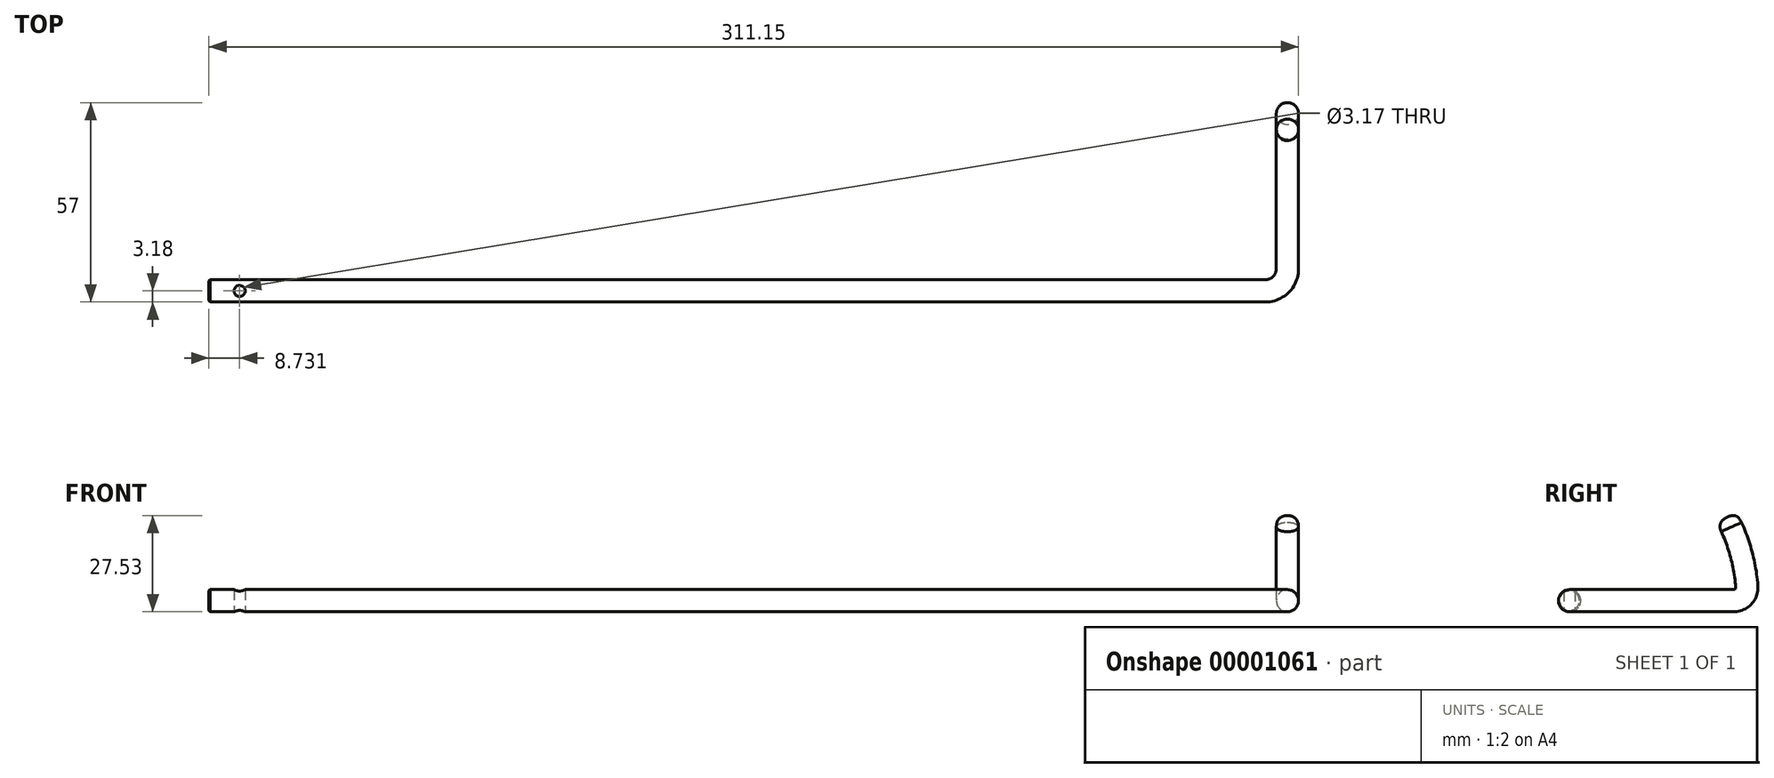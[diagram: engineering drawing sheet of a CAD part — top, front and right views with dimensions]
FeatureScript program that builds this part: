
annotation { "Feature Type Name" : "Feature", "Feature Type Description" : "" }
export const myFeature = defineFeature(function(context is Context, id is Id, definition is map)
    precondition{}
    {
        {
            var Q0;
            Q0=qCreatedBy(makeId("Top.planeOp"),FACE);
            var sketch = newSketch(context, id + "F0", { "sketchPlane" : qUnion([Q0])});
            skLineSegment(sketch, "E0", {"start": v(0, 0) * mm, "end": v(301.63, 0) * mm});
            skLineSegment(sketch, "E1", {"start": v(307.98, 6.35) * mm, "end": v(307.98, 50.8) * mm});
            skPoint(sketch, "E2.visualSharp", {"position": v(307.98, 0) * mm});
            skArc(sketch, "E2.filletArc", {"start": v(301.63, 0) * mm, "mid": v(306.12, 1.86) * mm, "end": v(307.98, 6.35) * mm});
            skLineSegment(sketch, "E3", {"start": v(307.98, 0) * mm, "end": v(301.63, 0) * mm, "construction": true});
            skSolve(sketch);
        }
        {
            var Q0;
            Q0=sQuery(id+"F0.wireOp",EDGE,"E3");
            var Q1;
            Q1=sQuery(id+"F0.wireOp",VERTEX,"E2.visualSharp");
            cPlane(context, id + "F1", {"entities" : qUnion([Q0, Q1]), "cplaneType" : CPlaneType.CURVE_POINT, "offset" : 152.4 * mm, "width" : 152.4 * mm, "height" : 152.4 * mm});
        }
        {
            var Q0;
            Q0=qCreatedBy(id+"F1.planeOp",FACE);
            var sketch = newSketch(context, id + "F2", { "sketchPlane" : qUnion([Q0])});
            skArc(sketch, "E4", {"start": v(-44.87, 23.81) * mm, "mid": v(-48.76, 14.26) * mm, "end": v(-50.63, 4.12) * mm});
            skArc(sketch, "E5", {"start": v(-50.63, 4.12) * mm, "mid": v(-49.64, 1.23) * mm, "end": v(-46.84, 0) * mm});
            skPoint(sketch, "E6.orphan", {"position": v(-50.8, 0) * mm});
            skSolve(sketch);
        }
        {
            var Q0;
            Q0=sQuery(id+"F2.wireOp",VERTEX,"E4.start");
            var Q1;
            Q1=sQuery(id+"F2.wireOp",EDGE,"E4");
            cPlane(context, id + "F3", {"entities" : qUnion([Q0, Q1]), "cplaneType" : CPlaneType.CURVE_POINT, "offset" : 152.4 * mm, "width" : 152.4 * mm, "height" : 152.4 * mm});
        }
        {
            var Q0;
            Q0=qCreatedBy(id+"F3.planeOp",FACE);
            var sketch = newSketch(context, id + "F4", { "sketchPlane" : qUnion([Q0])});
            skCircle(sketch, "E7", {"center": v(307.98, -50.8) * mm, "radius": 3.18 * mm});
            skSolve(sketch);
        }
        {
            var Q0;
            Q0=qCreatedBy(makeId("Right.planeOp"),FACE);
            var sketch = newSketch(context, id + "F5", { "sketchPlane" : qUnion([Q0])});
            skCircle(sketch, "E8", {"center": v(0, 0) * mm, "radius": 3.17 * mm});
            skSolve(sketch);
        }
        {
            var Q0;
            Q0=makeQuery(id+"F5.imprint","IMPRINT",FACE,{"disambiguationData":[TD([[makeQuery(id+"F5.imprint","IMPRINT",EDGE,{"derivedFrom":sQuery(id+"F5.wireOp",EDGE,"E8")}),1.0]])]});
            var Q1;
            Q1=sQuery(id+"F0.wireOp",EDGE,"E0");
            var Q2;
            Q2=sQuery(id+"F0.wireOp",EDGE,"E2.filletArc");
            sweep(context, id + "F6", {"profiles" : qUnion([Q0]), "path" : qUnion([Q1, Q2])});
        }
        {
            var Q0;
            Q0=makeQuery(id+"F4.imprint","IMPRINT",FACE,{"disambiguationData":[TD([[makeQuery(id+"F4.imprint","IMPRINT",EDGE,{"derivedFrom":sQuery(id+"F4.wireOp",EDGE,"E7")}),1.0]])]});
            var Q1;
            Q1=sQuery(id+"F2.wireOp",EDGE,"E4");
            var Q2;
            Q2=sQuery(id+"F2.wireOp",EDGE,"E5");
            sweep(context, id + "F7", {"profiles" : qUnion([Q0]), "path" : qUnion([Q1, Q2])});
        }
        {
            var Q0;
            Q0=makeQuery(id+"F7.opSweep","CAP_FACE",FACE,{"disambiguationData":[OSD([sQuery(id+"F2.wireOp",VERTEX,"E5.end"),sQuery(id+"F4.wireOp",EDGE,"E7")])],"isStart":false});
            extrude(context, id + "F8", {"entities" : qUnion([Q0]), "operationType" : NewBodyOperationType.ADD, "endBound" : BoundingType.UP_TO_NEXT, "depth" : 25.4 * mm});
        }
        {
            var Q0;
            Q0=makeQuery(id+"F7.opSweep","CAP_EDGE",EDGE,{"disambiguationData":[OSD([sQuery(id+"F2.wireOp",VERTEX,"E4.start"),sQuery(id+"F4.wireOp",EDGE,"E7")])],"isStart":true});
            fillet(context, id + "F9", {"entities" : qUnion([Q0]), "radius" : 3.05 * mm, "tangentPropagation" : true, "rho" : 0.5, "crossSection" : FilletCrossSection.CONIC, "allowEdgeOverflow" : false});
        }
        {
            var Q0;
            Q0=qCreatedBy(makeId("Top.planeOp"),FACE);
            var sketch = newSketch(context, id + "F10", { "sketchPlane" : qUnion([Q0])});
            skCircle(sketch, "E9", {"center": v(8.73, 0) * mm, "radius": 1.59 * mm});
            skSolve(sketch);
        }
        {
            var Q0;
            Q0=makeQuery(id+"F10.imprint","IMPRINT",FACE,{"disambiguationData":[TD([[makeQuery(id+"F10.imprint","IMPRINT",EDGE,{"derivedFrom":sQuery(id+"F10.wireOp",EDGE,"E9")}),1.0]])]});
            var Q1;
            Q1=sQuery(id+"F10.wireOp",EDGE,"E9");
            extrude(context, id + "F11", {"entities" : qUnion([Q0]), "operationType" : NewBodyOperationType.REMOVE, "surfaceEntities" : qUnion([Q1]), "depth" : 12.7 * mm, "symmetric" : true});
        }
        {
            var Q0;
            Q0=makeQuery(id+"F6.opSweep","CAP_EDGE",EDGE,{"disambiguationData":[OSD([sQuery(id+"F0.wireOp",VERTEX,"E0.start"),sQuery(id+"F5.wireOp",EDGE,"E8")])],"isStart":true});
            chamfer(context, id + "F12", {"entities" : qUnion([Q0]), "width" : 0.38 * mm, "tangentPropagation" : true});
        }
    });
